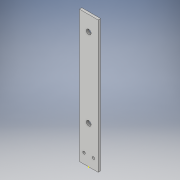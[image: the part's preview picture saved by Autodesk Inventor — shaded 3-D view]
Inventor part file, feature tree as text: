
AUTODESK INVENTOR PART (.ipt)
format: ipt  version: 2018 (Build 220112000, 112)  size: 104,960 bytes
history: native  units: in
note: dims shown in document units (in); Inventor stores cm internally (conversion verified against a paired STEP export)
features: sketch x2, extrude x1
ambient origin geometry x8: Origin, YZ Plane, XZ Plane, XY Plane, X Axis, Y Axis, Z Axis, Center Point
bodies: Solid1 (feature_tree)
feature tree (3):
  extrude  "Extrusion1"  Depth=13.7795in
  sketch  "Sketch2"  dims[d2=0.5in d3=0.5in d4=0.2559in d5=0.2559in d6=0.2559in d7=0.0in]
  sketch  "Sketch1"  dims[d0=1.9685in d1=13.7795in]
